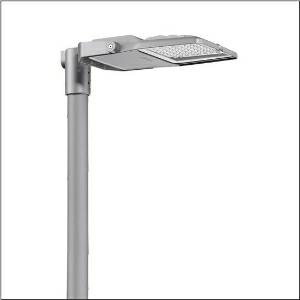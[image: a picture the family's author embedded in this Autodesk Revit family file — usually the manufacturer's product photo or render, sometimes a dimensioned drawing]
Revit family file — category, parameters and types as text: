
# Revit family: floodlight_fl_21_mini___pl33t_5xa7776d2f3a_276e
name_source: partatom
category: Lighting Fixtures
units: mm (PartAtom-declared; Revit-internal decimal feet)

## family parameters
Cut with Voids When Loaded = No
Host = Face
Light Source = No
Part Type = Normal
Room Calculation Point = No
Round Connector Dimension = Use Diameter
Shared = No

## types (1)
- --- (1 x LED, 17630 lm, 142.9 W, 3000K)
    Apparent Load = 143 VA
    CIE Flux Codes = 26 75 99 100 100
    Color Rendering = 70
    Color Temperature = 3000K
    Default Elevation = 1800 mm
    Description = Floodlight FL 21 mini, floodlight, primary light control with lens, of PMMA, primary optical cover: protective disc, of toughened safety glass, transparent, light distribution: PL33T, light emission: direct distribution, installation type: surface-mounted, LED, High Power LED, rated luminous flux: 17.630lm, luminous efficacy: 123lm/W, light colour: 730, colour temperature: 3000K, control gear: ECG Smart Interface, control: flexible luminous flux parameterisation, time-dependent luminous flux control, constant luminous flux control, overheat protection, presetting dimming logarithmic, with terminal, 6-pole, mains connection: 220..240V, AC, 50/60Hz, start of lifetime: 143W, end of lifetime: 151W, reduction: 63W, luminaire housing, of diecast aluminium, powder-coated, Siteco® metallic grey (DB 702S), corrosivity category C5 according to DIN EN ISO 12944, mast bracket, of steel, galvanised, powder-coated, Siteco® metallic grey (DB 702S), protection rating (complete): IP66, insulation class (complete): insulation class II (safety insulation), certification: CE, protection symbol: D, impact resistance: IK08, permissible operating ambient temperature: -40..+40°C, permissible operating ambient temperature for outdoor applications: -40..+50°C, standard: DIN EN 12944, packaging unit: 1 piece

Light Distribution: PL33T
    Height = 70 mm
    Lamp = 1 x LED
    Lamp Light Flux = 17630 lm
    Lamp Power = 142.9 W
    Lamp count = 1
    Length = 485 mm
    Luminous efficacy = 123 lm/W
    Manufacturer = Siteco
    ModVariant = No
    Model = 5XA7776D2F3A
    Number of Poles = 1
    OnlyDefault = Yes
    Power Factor = 1
    Product Name = Floodlight FL 21 mini | PL33T
    Product group = floodlight | pylon top
    ProductGroupID = 6101
    Protection Class = Protection class II
    Protection Degree = IP 66
    RLX_Detail_Level = 1
    RlxData = <blob elided: 100869 chars, md5=f136fe16>
    Socket = socket
    Standby Power = 0 W
    System Light Flux = 17630 lm
    System Power = 143 W
    Type Comments = factory setting: luminous flux: 100 % | dim-lin: 254 | 730 mA
    Type Image = l_1007125.jpg
    URL = http://relux.com
    VarID = @adj_058423
    Voltage = 0 V
    Weight = 0.00 kg
    Width = 337 mm

## geometry (parser evidence)
native form markers: Blend x4, Sweep x11
no freeform markers — native parametric forms only
